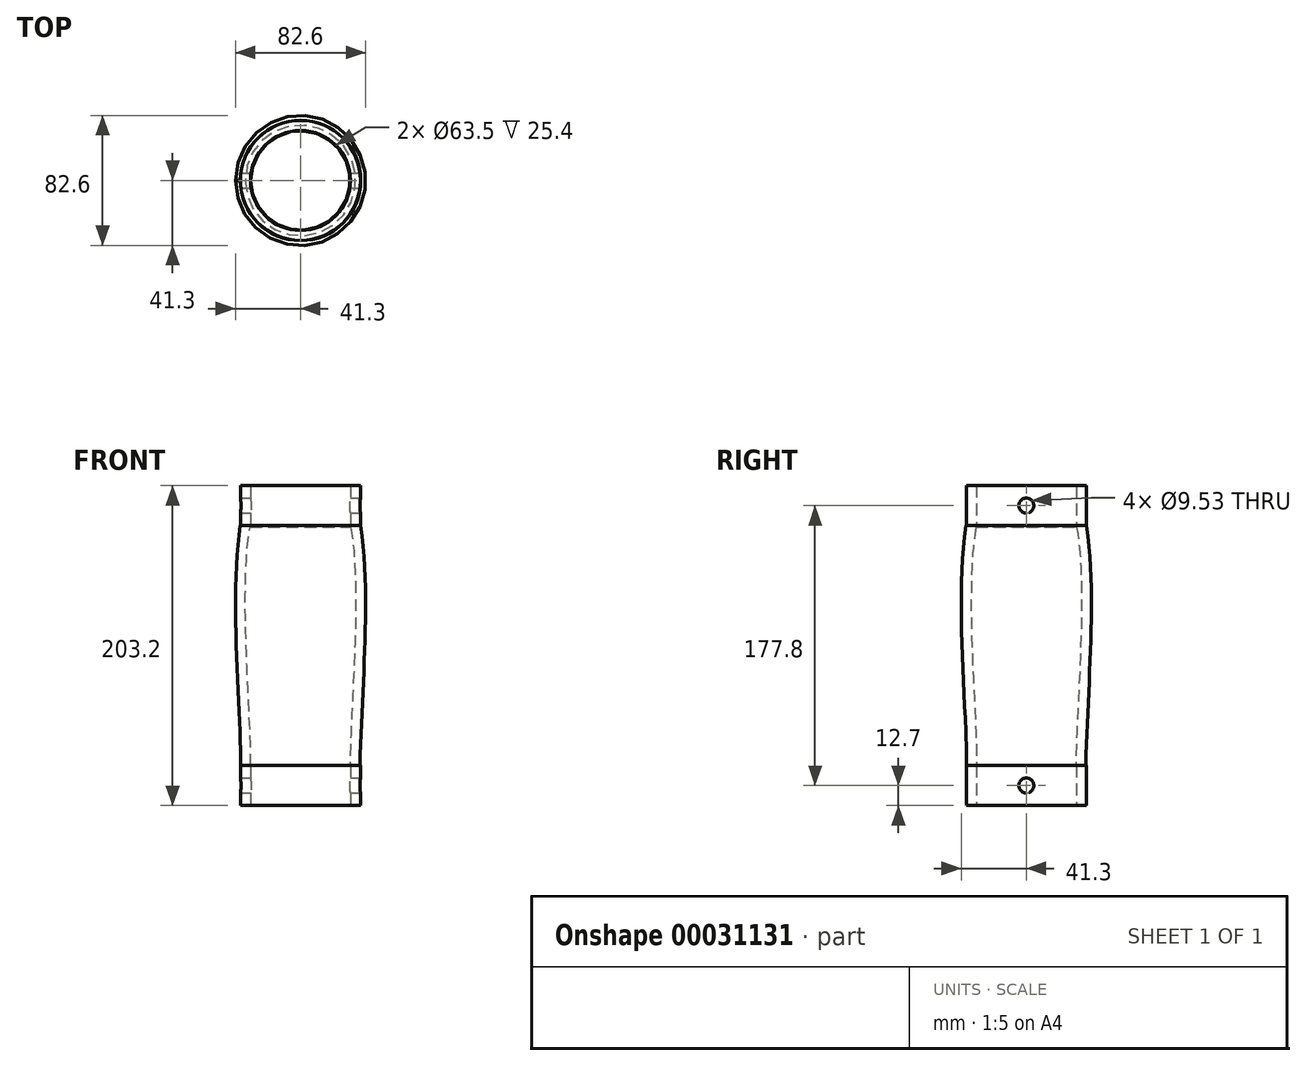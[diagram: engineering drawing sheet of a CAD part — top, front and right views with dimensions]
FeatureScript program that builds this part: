
annotation { "Feature Type Name" : "Feature", "Feature Type Description" : "" }
export const myFeature = defineFeature(function(context is Context, id is Id, definition is map)
    precondition{}
    {
        {
            var Q0;
            Q0=qCreatedBy(makeId("Top.planeOp"),FACE);
            var sketch = newSketch(context, id + "F0", { "sketchPlane" : qUnion([Q0])});
            skCircle(sketch, "E0", {"center": v(0, 0) * mm, "radius": 31.75 * mm});
            skCircle(sketch, "E1", {"center": v(0, 0) * mm, "radius": 38.1 * mm});
            skSolve(sketch);
        }
        {
            var Q0;
            Q0 = qSketchRegion(id + "F0", true);
            extrude(context, id + "F1", {"entities" : qUnion([Q0]), "depth" : 25.4 * mm});
        }
        {
            var Q0;
            Q0=qCreatedBy(makeId("Front.planeOp"),FACE);
            var sketch = newSketch(context, id + "F2", { "sketchPlane" : qUnion([Q0])});
            skLineSegment(sketch, "E2", {"start": v(0, 0) * mm, "end": v(0, 86.1) * mm, "construction": true});
            skFitSpline(sketch, "E3", {"points": [v(-37.9, 25.4) * mm, v(-38.21, 177.8) * mm], "startDerivative": vector(0, 107.78) * mm, "endDerivative": vector(21.4, 134.41) * mm});
            skFitSpline(sketch, "E4.0", {"points": [v(-31.56, 25.4) * mm, v(-31.56, 30) * mm, v(-31.8, 40.23) * mm, v(-32.59, 58.07) * mm, v(-33.56, 77.7) * mm, v(-34.44, 98.43) * mm, v(-35, 119.5) * mm, v(-34.96, 140.19) * mm, v(-34.1, 159.7) * mm, v(-32.8, 171.42) * mm, v(-31.94, 176.8) * mm]});
            skLineSegment(sketch, "E5", {"start": v(-37.9, 25.4) * mm, "end": v(-31.56, 25.4) * mm});
            skLineSegment(sketch, "E6", {"start": v(-38.21, 177.8) * mm, "end": v(-31.65, 177.8) * mm});
            skLineSegment(sketch, "E7", {"start": v(-31.65, 177.8) * mm, "end": v(-31.94, 176.8) * mm});
            skSolve(sketch);
        }
        {
            var Q0;
            Q0=makeQuery(id+"F2.imprint","IMPRINT",FACE,{"disambiguationData":[TD([[makeQuery(id+"F2.imprint","IMPRINT",EDGE,{"derivedFrom":sQuery(id+"F2.wireOp",EDGE,"E3")}),-1.0]])]});
            var Q1;
            Q1=sQuery(id+"F2.wireOp",EDGE,"E2");
            revolve(context, id + "F3", {"operationType" : NewBodyOperationType.ADD, "entities" : qUnion([Q0]), "axis" : qUnion([Q1]), "revolveType" : RevolveType.FULL});
        }
        {
            var Q0;
            Q0=qCreatedBy(makeId("Top.planeOp"),FACE);
            cPlane(context, id + "F4", {"entities" : qUnion([Q0]), "cplaneType" : CPlaneType.OFFSET, "offset" : 177.8 * mm, "width" : 152.4 * mm, "height" : 152.4 * mm});
        }
        {
            var Q0;
            Q0=qCreatedBy(id+"F4.planeOp",FACE);
            var sketch = newSketch(context, id + "F5", { "sketchPlane" : qUnion([Q0])});
            skCircle(sketch, "E8", {"center": v(0, 0) * mm, "radius": 38.1 * mm});
            skCircle(sketch, "E9", {"center": v(0, 0) * mm, "radius": 31.75 * mm});
            skSolve(sketch);
        }
        {
            var Q0;
            Q0=makeQuery(id+"F5.imprint","IMPRINT",FACE,{"disambiguationData":[TD([[makeQuery(id+"F5.imprint","IMPRINT",EDGE,{"derivedFrom":sQuery(id+"F5.wireOp",EDGE,"E8")}),1.0]])]});
            extrude(context, id + "F6", {"entities" : qUnion([Q0]), "operationType" : NewBodyOperationType.ADD, "depth" : 25.4 * mm});
        }
        {
            var Q0;
            Q0=qCreatedBy(makeId("Right.planeOp"),FACE);
            var sketch = newSketch(context, id + "F7", { "sketchPlane" : qUnion([Q0])});
            skLineSegment(sketch, "E10", {"start": v(0, 66.9) * mm, "end": v(0, 137.3) * mm, "construction": true});
            skCircle(sketch, "E11", {"center": v(0, 190.5) * mm, "radius": 4.76 * mm});
            skLineSegment(sketch, "E12", {"start": v(-89.84, 101.6) * mm, "end": v(60.03, 101.6) * mm, "construction": true});
            skCircle(sketch, "E13.MirrorC", {"center": v(0, 12.7) * mm, "radius": 4.76 * mm});
            skLineSegment(sketch, "E14", {"start": v(0, 170.47) * mm, "end": v(0, 210.53) * mm, "construction": true});
            skLineSegment(sketch, "E15", {"start": v(-20.15, 190.5) * mm, "end": v(45.4, 190.5) * mm, "construction": true});
            skSolve(sketch);
        }
        {
            var Q0;
            Q0 = qSketchRegion(id + "F7", true);
            extrude(context, id + "F8", {"entities" : qUnion([Q0]), "operationType" : NewBodyOperationType.REMOVE, "endBound" : BoundingType.THROUGH_ALL, "oppositeDirection" : true, "depth" : 25.4 * mm, "hasSecondDirection" : true, "secondDirectionBound" : SecondDirectionBoundingType.THROUGH_ALL, "secondDirectionOppositeDirection" : false, "secondDirectionDepth" : 25.4 * mm});
        }
    });
